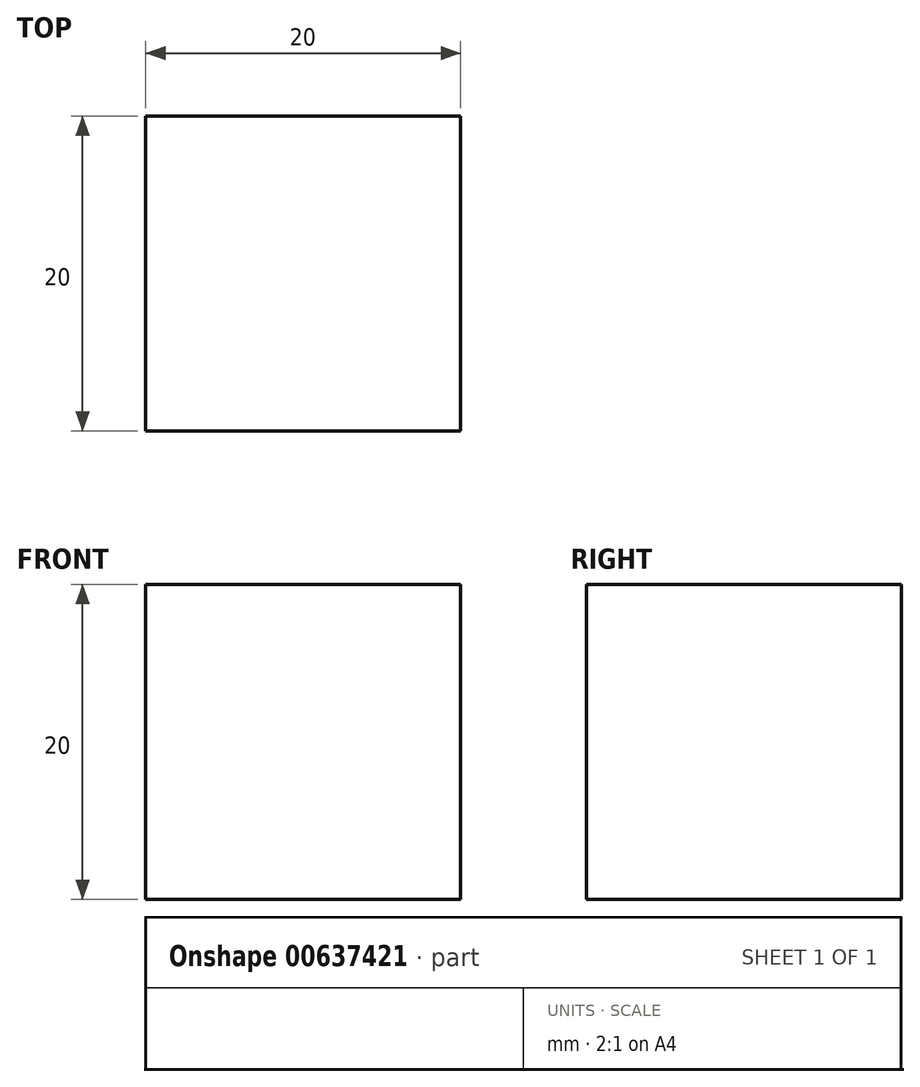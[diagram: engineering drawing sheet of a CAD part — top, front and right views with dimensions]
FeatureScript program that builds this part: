
annotation { "Feature Type Name" : "Feature", "Feature Type Description" : "" }
export const myFeature = defineFeature(function(context is Context, id is Id, definition is map)
    precondition{}
    {
        {
            var Q0;
            Q0=qCreatedBy(makeId("Front.planeOp"),FACE);
            var sketch = newSketch(context, id + "F0", { "sketchPlane" : qUnion([Q0])});
            skLineSegment(sketch, "E0.bottom", {"start": v(1.52, 16.46) * mm, "end": v(21.52, 16.46) * mm});
            skLineSegment(sketch, "E0.top", {"start": v(1.52, -3.54) * mm, "end": v(21.52, -3.54) * mm});
            skLineSegment(sketch, "E0.left", {"start": v(1.52, 16.46) * mm, "end": v(1.52, -3.54) * mm});
            skLineSegment(sketch, "E0.right", {"start": v(21.52, 16.46) * mm, "end": v(21.52, -3.54) * mm});
            skSolve(sketch);
        }
        {
            var Q0;
            Q0 = qSketchRegion(id + "F0", true);
            extrude(context, id + "F1", {"entities" : qUnion([Q0]), "depth" : 20 * mm, "offsetDistance" : 25 * mm});
        }
    });
